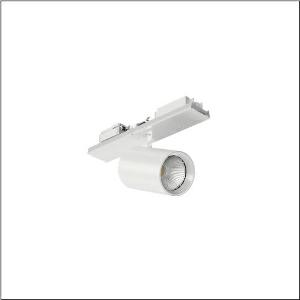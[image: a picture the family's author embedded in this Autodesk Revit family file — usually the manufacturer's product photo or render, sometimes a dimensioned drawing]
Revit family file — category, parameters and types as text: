
# Revit family: licross_r__spot_31_51sl14da43b_e1eb
name_source: partatom
category: Lighting Fixtures
units: mm (PartAtom-declared; Revit-internal decimal feet)

## family parameters
Cut with Voids When Loaded = No
Host = Face
Light Source = No
Part Type = Normal
Room Calculation Point = No
Round Connector Dimension = Use Diameter
Shared = No

## types (1)
- --- (1 x LED, 3720 lm, 28.5 W, 4000K)
    Apparent Load = 29 VA
    CIE Flux Codes = 93 97 100 100 100
    Color Rendering = 90
    Color Temperature = 4000K
    Default Elevation = 1800 mm
    Description = Licross® Spot 31, directional spotlight, light control with lens, of plastic, LED rated luminous flux: 3.720lm, light colour: 940, with plug, 5-pole, mains connection: 220..240V, AC, 50/60Hz, of aluminium, traffic white (RAL 9016), length: 140mm, diameter: 90mm, protection rating (complete): IP20, insulation class (complete): insulation class I (protective earthing), certification: CE, packaging unit: 1 piece
    Height = 175 mm
    Lamp = 1 x LED
    Lamp Light Flux = 3720 lm
    Lamp Power = 28.5 W
    Lamp count = 1
    Length = 90 mm
    Luminous efficacy = 131 lm/W
    Manufacturer = Siteco
    ModVariant = No
    Model = 51SL14DA43B
    Mounting Place = Ceiling
    Mounting Type = Pendant
    Number of Poles = 1
    OnlyDefault = Yes
    Power Factor = 1
    Product Name = Licross® Spot 31
    Product group = directional spotlight
    ProductGroupID = 905
    Protection Class = Protection class I
    Protection Degree = IP 20
    RLX_Detail_Level = 1
    RLX_Emergency_Light_Flux = 0 lm
    RLX_Emergency_Type = 0
    RLX_Emergency_Type_DB = No
    RlxData = <blob elided: 14793 chars, md5=943e663a>
    Socket = socket
    Standby Power = 0 W
    System Light Flux = 3720 lm
    System Power = 29 W
    Type Comments = factory setting: luminous flux: 100 % | (ON | ON | ON) | 700 mA
    Type Image = l_1245720.jpg
    URL = http://relux.com
    VarID = @adj_081683
    Voltage = 0 V
    Weight = 0.00 kg
    Width = 0 mm  [stored 0 ft]

note: [stored X ft] marks values corroborated as IEEE doubles in the binary element streams (Revit-internal decimal feet)

## geometry (parser evidence)
native form markers: Sweep x11
no freeform markers — native parametric forms only
